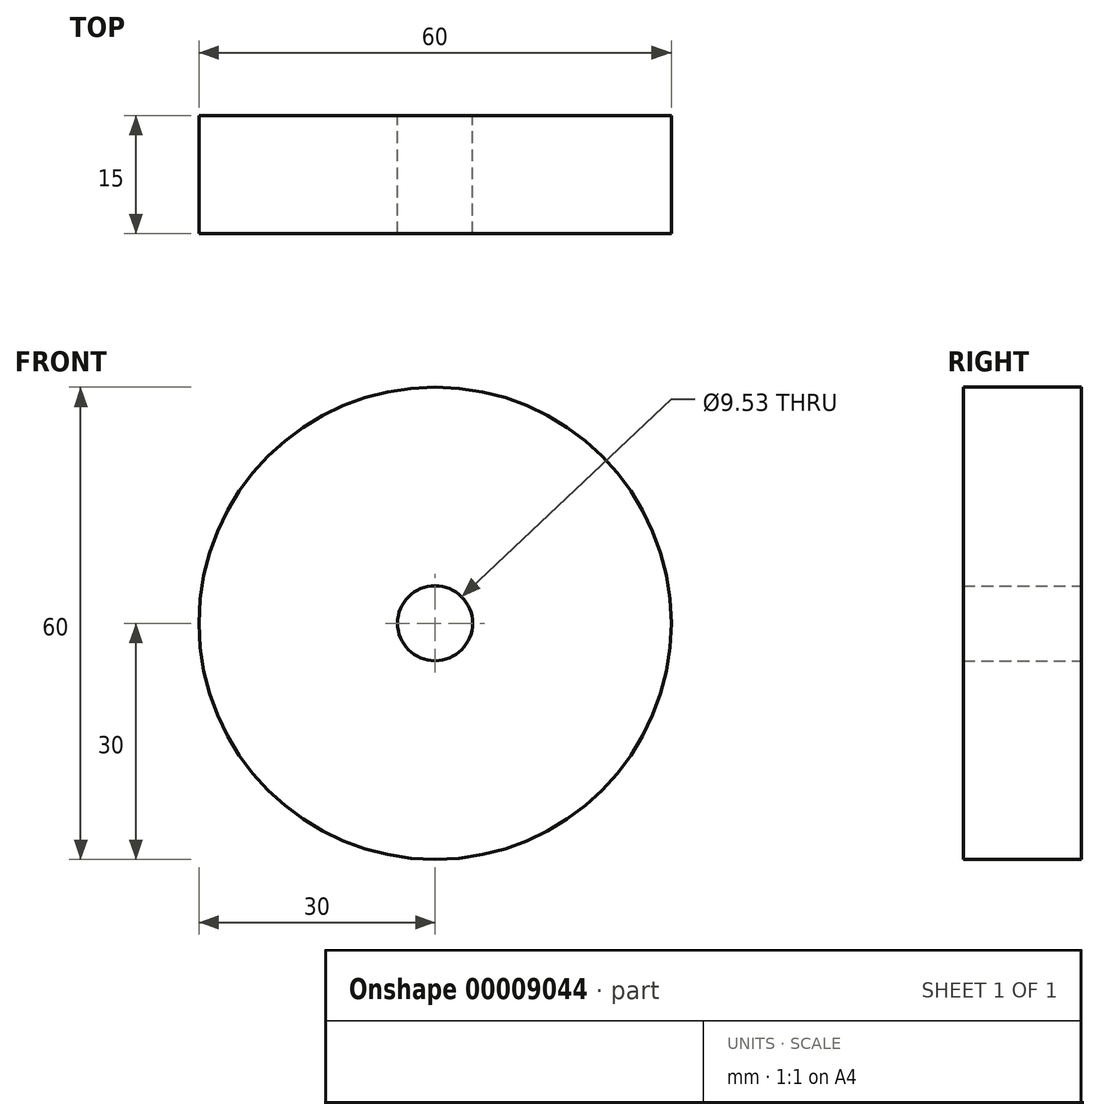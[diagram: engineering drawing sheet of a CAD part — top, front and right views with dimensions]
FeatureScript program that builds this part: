
annotation { "Feature Type Name" : "Feature", "Feature Type Description" : "" }
export const myFeature = defineFeature(function(context is Context, id is Id, definition is map)
    precondition{}
    {
        {
            var Q0;
            Q0=qCreatedBy(makeId("Front.planeOp"),FACE);
            var sketch = newSketch(context, id + "F0", { "sketchPlane" : qUnion([Q0])});
            skCircle(sketch, "E0", {"center": v(0, 0) * mm, "radius": 30 * mm});
            skCircle(sketch, "E1", {"center": v(0, 0) * mm, "radius": 4.76 * mm});
            skSolve(sketch);
        }
        {
            var Q0;
            Q0 = qSketchRegion(id + "F0", true);
            extrude(context, id + "F1", {"entities" : qUnion([Q0]), "depth" : 15 * mm});
        }
    });
